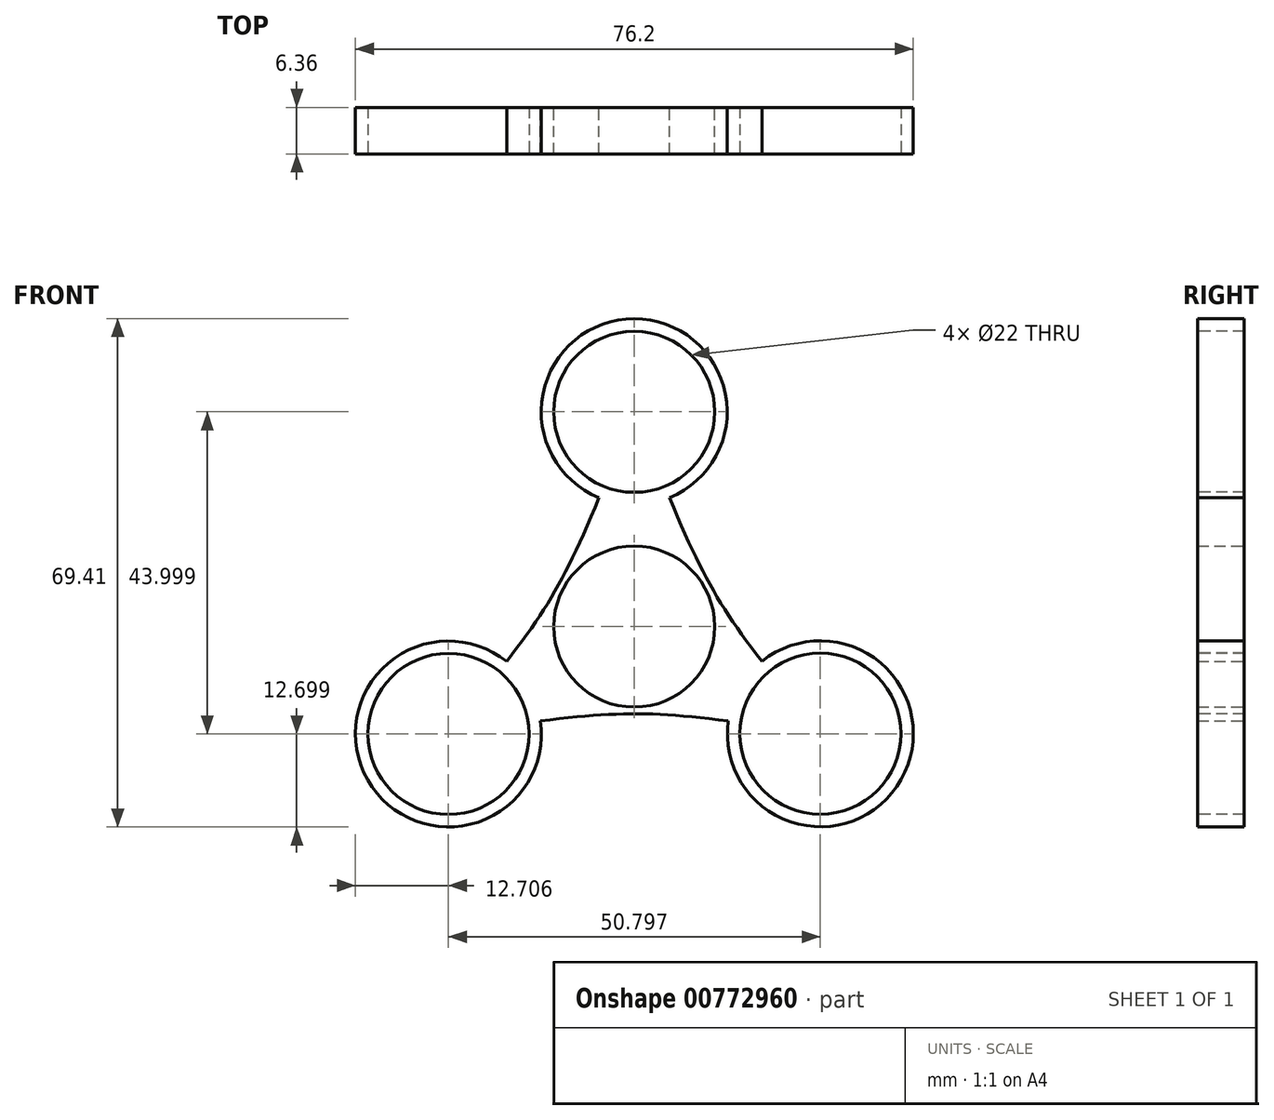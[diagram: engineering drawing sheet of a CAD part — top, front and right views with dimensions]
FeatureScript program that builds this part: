
annotation { "Feature Type Name" : "Feature", "Feature Type Description" : "" }
export const myFeature = defineFeature(function(context is Context, id is Id, definition is map)
    precondition{}
    {
        {
            var Q0;
            Q0=qCreatedBy(makeId("Front.planeOp"),FACE);
            var sketch = newSketch(context, id + "F0", { "sketchPlane" : qUnion([Q0])});
            skCircle(sketch, "E0", {"center": v(0, 45.02) * mm, "radius": 12.7 * mm});
            skCircle(sketch, "E1", {"center": v(-25.38, 1) * mm, "radius": 12.7 * mm});
            skCircle(sketch, "E2", {"center": v(25.42, 1.04) * mm, "radius": 12.7 * mm});
            skCircle(sketch, "E3", {"center": v(0, 15.68) * mm, "radius": 11 * mm});
            skFitSpline(sketch, "E4", {"points": [v(-25.38, 1) * mm, v(0, 45.02) * mm], "startDerivative": vector(45.23, 55.61) * mm, "endDerivative": vector(30.9, 76.41) * mm});
            skFitSpline(sketch, "E5", {"points": [v(0, 45.02) * mm, v(25.42, 1.04) * mm], "startDerivative": vector(30.79, -76.13) * mm, "endDerivative": vector(45.49, -55.8) * mm});
            skFitSpline(sketch, "E6", {"points": [v(25.42, 1.04) * mm, v(-25.38, 1) * mm], "startDerivative": vector(-76.27, 10.92) * mm, "endDerivative": vector(-76.13, -11) * mm});
            skSolve(sketch);
        }
        {
            var Q0;
            Q0=qCreatedBy(makeId("Front.planeOp"),FACE);
            var sketch = newSketch(context, id + "F1", { "sketchPlane" : qUnion([Q0])});
            skCircle(sketch, "E7", {"center": v(0, 45) * mm, "radius": 11 * mm});
            skCircle(sketch, "E8", {"center": v(25.42, 1.05) * mm, "radius": 11 * mm});
            skCircle(sketch, "E9", {"center": v(-25.37, 1) * mm, "radius": 11 * mm});
            skSolve(sketch);
        }
        {
            var Q0;
            Q0 = qSketchRegion(id + "F0", true);
            extrude(context, id + "F2", {"entities" : qUnion([Q0]), "endBound" : BoundingType.SYMMETRIC, "depth" : 6.35 * mm, "offsetDistance" : 25.4 * mm});
        }
        {
            var Q0;
            Q0 = qSketchRegion(id + "F1", true);
            extrude(context, id + "F3", {"entities" : qUnion([Q0]), "operationType" : NewBodyOperationType.REMOVE, "endBound" : BoundingType.SYMMETRIC, "oppositeDirection" : true, "depth" : 25.4 * mm, "offsetDistance" : 25.4 * mm});
        }
    });
